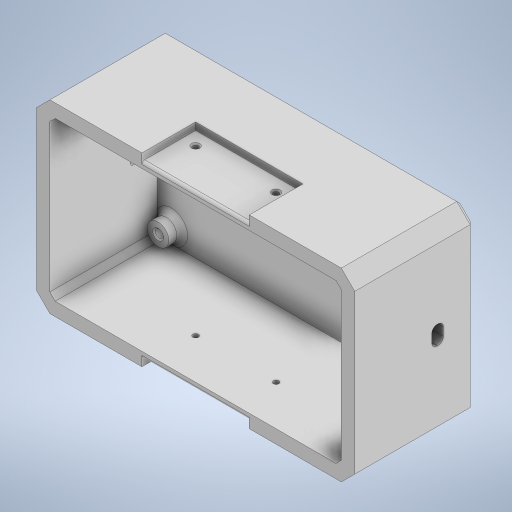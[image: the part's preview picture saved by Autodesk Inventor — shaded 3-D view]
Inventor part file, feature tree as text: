
AUTODESK INVENTOR PART (.ipt)
format: ipt  version: 2023 (Build 270158000, 158)  size: 362,496 bytes
history: native  units: mm
features: extrude x7, sketch x5, fillet x4, chamfer x4, projected_geometry x3, other x2, hole x1
ambient origin geometry x8: Origin, YZ Plane, XZ Plane, XY Plane, X Axis, Y Axis, Z Axis, Center Point
bodies: Body1 (feature_tree)
feature tree (26):
  other  "솔리드1"
  sketch  "스케치1"
  extrude  "돌출1"  Depth=108.6mm
  extrude  "돌출2"  Depth=59.0mm
  extrude  "돌출4"  Depth=8.0mm
  hole  "구멍1"  [1 undecoded]
  fillet  "모깎기2"  Radius=47.5mm
  other  "작업 평면1"
  sketch  "스케치3"
  extrude  "돌출5"  Depth=98.0mm
  extrude  "돌출6"  Depth=5.0mm TaperAngle=0.0deg
  fillet  "모깎기4"  Radius=40.0mm
  fillet  "모깎기6"  Radius=5.0mm
  extrude  "돌출7"  Depth=2.0mm
  extrude  "돌출8"  Depth=7.0mm
  chamfer  "모따기1"  Distance=4.0mm
  chamfer  "모따기2"  Distance=7.0mm
  chamfer  "모따기3"  Distance=4.3mm
  fillet  "모깎기7"  Radius=3.0mm
  chamfer  "모따기4"  Distance=2.0mm
  sketch  "스케치2"
  projected_geometry  "투영된 루프1"
  projected_geometry  "투영된 루프2"
  projected_geometry  "투영된 루프3"
  sketch  "스케치4"
  sketch  "스케치5"
note: 1 required parameter value undecoded (feature->parameter linkage not recoverable at this tier; creation-order binding heuristic only, values carry confidence <= 0.55)
